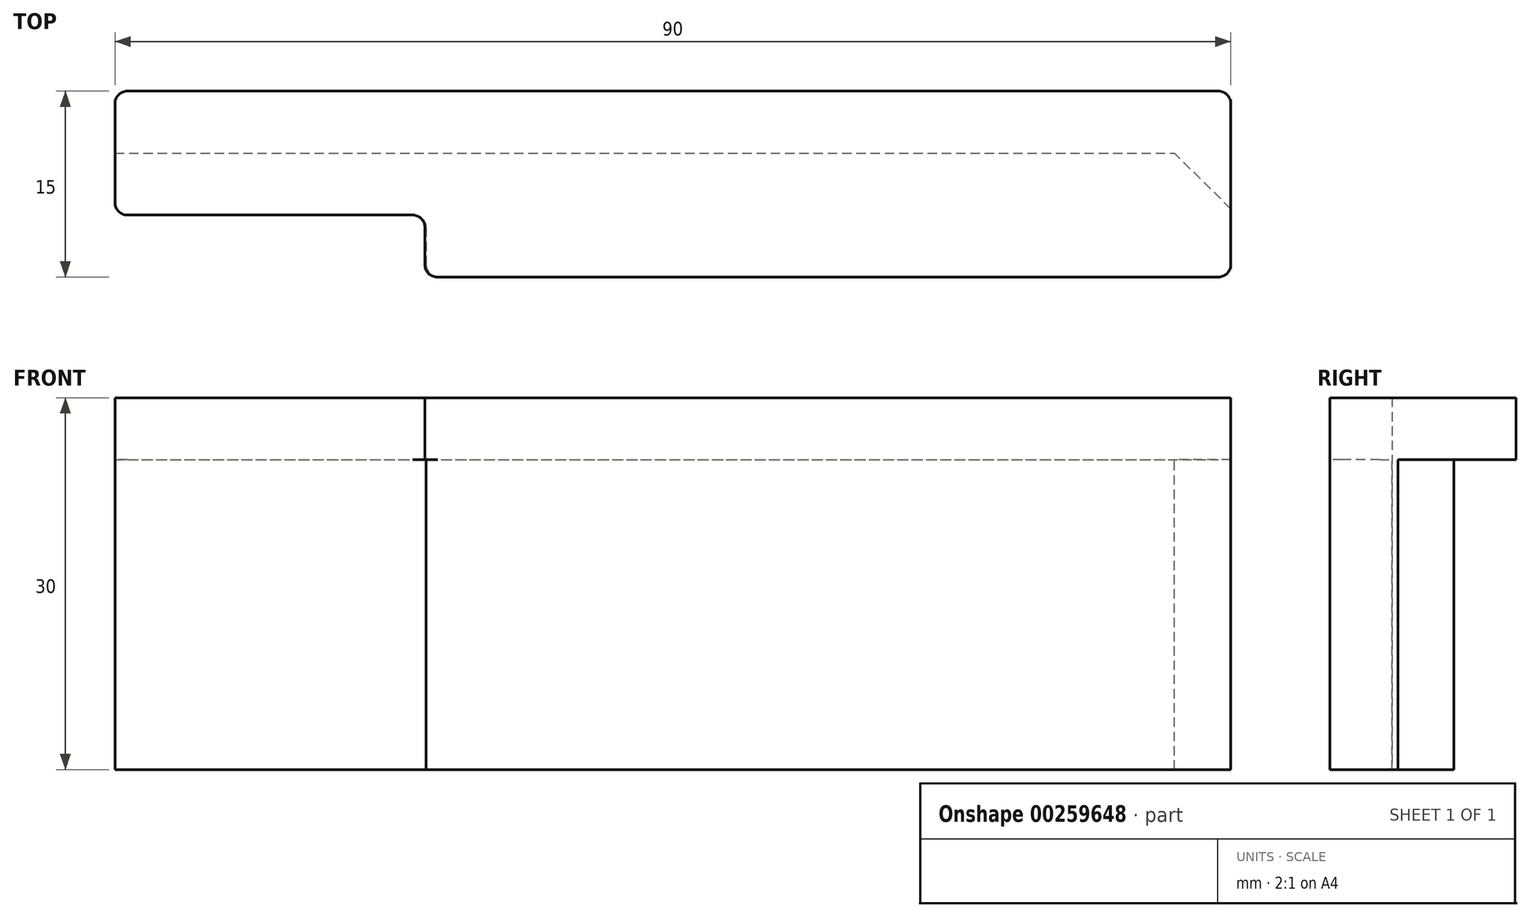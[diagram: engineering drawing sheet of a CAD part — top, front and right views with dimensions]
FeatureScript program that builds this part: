
annotation { "Feature Type Name" : "Feature", "Feature Type Description" : "" }
export const myFeature = defineFeature(function(context is Context, id is Id, definition is map)
    precondition{}
    {
        {
            var Q0;
            Q0=qCreatedBy(makeId("Top.planeOp"),FACE);
            var sketch = newSketch(context, id + "F0", { "sketchPlane" : qUnion([Q0])});
            skLineSegment(sketch, "E0.bottom", {"start": v(-31.5, -7.5) * mm, "end": v(31.5, -7.5) * mm});
            skLineSegment(sketch, "E0.top", {"start": v(-32.5, 7.5) * mm, "end": v(31.5, 7.5) * mm});
            skLineSegment(sketch, "E0.left", {"start": v(-32.5, -6.5) * mm, "end": v(-32.5, -3.5) * mm});
            skLineSegment(sketch, "E0.right", {"start": v(32.5, -6.5) * mm, "end": v(32.5, 6.5) * mm});
            skLineSegment(sketch, "E1", {"start": v(-32.5, 7.5) * mm, "end": v(-56.5, 7.5) * mm});
            skLineSegment(sketch, "E2", {"start": v(-57.5, 6.5) * mm, "end": v(-57.5, -1.5) * mm});
            skLineSegment(sketch, "E3", {"start": v(-56.5, -2.5) * mm, "end": v(-33.5, -2.5) * mm});
            skPoint(sketch, "E4.visualSharp", {"position": v(-57.5, 7.5) * mm});
            skArc(sketch, "E4.filletArc", {"start": v(-56.5, 7.5) * mm, "mid": v(-57.2, 7.2) * mm, "end": v(-57.5, 6.5) * mm});
            skPoint(sketch, "E5.visualSharp", {"position": v(-57.5, -2.5) * mm});
            skArc(sketch, "E5.filletArc", {"start": v(-57.5, -1.5) * mm, "mid": v(-57.2, -2.2) * mm, "end": v(-56.5, -2.5) * mm});
            skPoint(sketch, "E6.visualSharp", {"position": v(-32.5, -2.5) * mm});
            skArc(sketch, "E6.filletArc", {"start": v(-32.5, -3.5) * mm, "mid": v(-32.8, -2.8) * mm, "end": v(-33.5, -2.5) * mm});
            skPoint(sketch, "E7.visualSharp", {"position": v(-32.5, -7.5) * mm});
            skArc(sketch, "E7.filletArc", {"start": v(-32.5, -6.5) * mm, "mid": v(-32.2, -7.2) * mm, "end": v(-31.5, -7.5) * mm});
            skPoint(sketch, "E8.visualSharp", {"position": v(32.5, -7.5) * mm});
            skArc(sketch, "E8.filletArc", {"start": v(31.5, -7.5) * mm, "mid": v(32.2, -7.2) * mm, "end": v(32.5, -6.5) * mm});
            skPoint(sketch, "E9.visualSharp", {"position": v(32.5, 7.5) * mm});
            skArc(sketch, "E9.filletArc", {"start": v(32.5, 6.5) * mm, "mid": v(32.2, 7.2) * mm, "end": v(31.5, 7.5) * mm});
            skSolve(sketch);
        }
        {
            var Q0;
            Q0=makeQuery(id+"F0.imprint","IMPRINT",FACE,{"disambiguationData":[TD([[makeQuery(id+"F0.imprint","IMPRINT",EDGE,{"derivedFrom":sQuery(id+"F0.wireOp",EDGE,"E0.bottom")}),1.0]])]});
            extrude(context, id + "F1", {"entities" : qUnion([Q0]), "depth" : 5 * mm});
        }
        {
            var Q0;
            Q0=makeQuery(id+"F1.opExtrude","CAP_FACE",FACE,{"disambiguationData":[OSD([sQuery(id+"F0.wireOp",EDGE,"E0.bottom"),sQuery(id+"F0.wireOp",EDGE,"E0.top"),sQuery(id+"F0.wireOp",EDGE,"E0.left"),sQuery(id+"F0.wireOp",EDGE,"E0.right"),sQuery(id+"F0.wireOp",EDGE,"E1"),sQuery(id+"F0.wireOp",EDGE,"E2"),sQuery(id+"F0.wireOp",EDGE,"E3"),sQuery(id+"F0.wireOp",EDGE,"E4.filletArc"),sQuery(id+"F0.wireOp",EDGE,"E5.filletArc"),sQuery(id+"F0.wireOp",EDGE,"E6.filletArc"),sQuery(id+"F0.wireOp",EDGE,"E7.filletArc"),sQuery(id+"F0.wireOp",EDGE,"E8.filletArc"),sQuery(id+"F0.wireOp",EDGE,"E9.filletArc")])],"isStart":true});
            var sketch = newSketch(context, id + "F2", { "sketchPlane" : qUnion([Q0])});
            skLineSegment(sketch, "E10.bottom", {"start": v(-57.5, -2.5) * mm, "end": v(27.95, -2.5) * mm});
            skLineSegment(sketch, "E10.top", {"start": v(-31.4, 7.5) * mm, "end": v(31.5, 7.5) * mm});
            skLineSegment(sketch, "E10.left", {"start": v(-57.5, -2.5) * mm, "end": v(-57.5, 1.5) * mm});
            skLineSegment(sketch, "E10.right", {"start": v(32.5, 2) * mm, "end": v(32.5, 6.5) * mm});
            skLineSegment(sketch, "E11", {"start": v(-56.5, 2.5) * mm, "end": v(-33.4, 2.5) * mm});
            skLineSegment(sketch, "E12", {"start": v(-32.4, 3.5) * mm, "end": v(-32.4, 6.5) * mm});
            skPoint(sketch, "E13.orphan", {"position": v(-57.5, 7.5) * mm});
            skPoint(sketch, "E14.visualSharp", {"position": v(-57.5, 2.5) * mm});
            skArc(sketch, "E14.filletArc", {"start": v(-56.5, 2.5) * mm, "mid": v(-57.2, 2.2) * mm, "end": v(-57.5, 1.5) * mm});
            skPoint(sketch, "E15.visualSharp", {"position": v(-32.4, 2.5) * mm});
            skArc(sketch, "E15.filletArc", {"start": v(-33.4, 2.5) * mm, "mid": v(-32.7, 2.8) * mm, "end": v(-32.4, 3.5) * mm});
            skPoint(sketch, "E16.visualSharp", {"position": v(-32.4, 7.5) * mm});
            skArc(sketch, "E16.filletArc", {"start": v(-31.4, 7.5) * mm, "mid": v(-32.1, 7.2) * mm, "end": v(-32.4, 6.5) * mm});
            skPoint(sketch, "E17.visualSharp", {"position": v(32.5, 7.5) * mm});
            skArc(sketch, "E17.filletArc", {"start": v(32.5, 6.5) * mm, "mid": v(32.2, 7.2) * mm, "end": v(31.5, 7.5) * mm});
            skLineSegment(sketch, "E18", {"start": v(32.5, 2) * mm, "end": v(27.95, -2.5) * mm});
            skPoint(sketch, "E19.orphan", {"position": v(32.5, -2.5) * mm});
            skSolve(sketch);
        }
        {
            var Q0;
            Q0=makeQuery(id+"F2.imprint","IMPRINT",FACE,{"disambiguationData":[TD([[makeQuery(id+"F2.imprint","IMPRINT",EDGE,{"derivedFrom":sQuery(id+"F2.wireOp",EDGE,"E10.bottom")}),1.0]])]});
            extrude(context, id + "F3", {"entities" : qUnion([Q0]), "operationType" : NewBodyOperationType.ADD, "depth" : 25 * mm});
        }
    });
